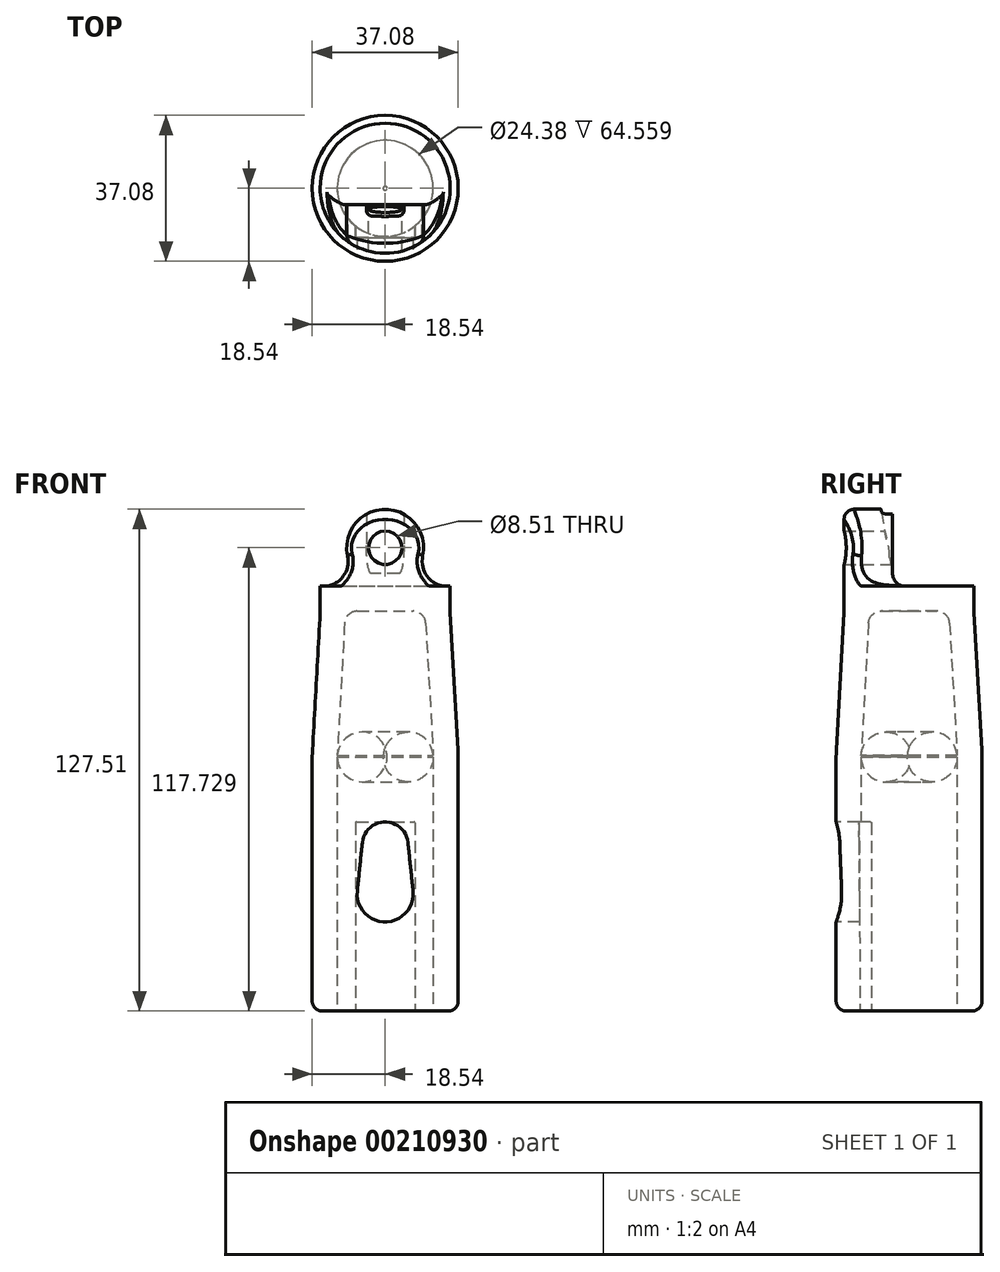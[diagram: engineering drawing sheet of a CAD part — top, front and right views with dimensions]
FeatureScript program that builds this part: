
annotation { "Feature Type Name" : "Feature", "Feature Type Description" : "" }
export const myFeature = defineFeature(function(context is Context, id is Id, definition is map)
    precondition{}
    {
        {
            var Q0;
            Q0=qCreatedBy(makeId("Front.planeOp"),FACE);
            var sketch = newSketch(context, id + "F0", { "sketchPlane" : qUnion([Q0])});
            skLineSegment(sketch, "E0", {"start": v(-18.54, -101.6) * mm, "end": v(-18.54, -38.1) * mm});
            skLineSegment(sketch, "E1", {"start": v(-18.46, -35.28) * mm, "end": v(-16.52, -0.35) * mm});
            skLineSegment(sketch, "E2", {"start": v(-16.51, 0) * mm, "end": v(-16.51, 6.35) * mm});
            skLineSegment(sketch, "E3", {"start": v(-16.51, 6.35) * mm, "end": v(0, 6.35) * mm});
            skLineSegment(sketch, "E4", {"start": v(-10.3, -3) * mm, "end": v(-12.18, -36.69) * mm});
            skLineSegment(sketch, "E5", {"start": v(-12.2, -37.04) * mm, "end": v(-12.2, -101.6) * mm});
            skLineSegment(sketch, "E6", {"start": v(-12.2, -101.6) * mm, "end": v(-18.54, -101.6) * mm});
            skLineSegment(sketch, "E7", {"start": v(0, 0) * mm, "end": v(0, 33.96) * mm, "construction": true});
            skLineSegment(sketch, "E8", {"start": v(0, 6.35) * mm, "end": v(0, 0) * mm});
            skLineSegment(sketch, "E9", {"start": v(0, 0) * mm, "end": v(-7.14, 0) * mm});
            skPoint(sketch, "E10.visualSharp", {"position": v(-16.51, -0.18) * mm});
            skArc(sketch, "E10.filletArc", {"start": v(-16.52, -0.35) * mm, "mid": v(-16.51, -0.18) * mm, "end": v(-16.51, 0) * mm});
            skPoint(sketch, "E11.visualSharp", {"position": v(-18.54, -36.69) * mm});
            skArc(sketch, "E11.filletArc", {"start": v(-18.46, -35.28) * mm, "mid": v(-18.52, -36.69) * mm, "end": v(-18.54, -38.1) * mm});
            skPoint(sketch, "E12.visualSharp", {"position": v(-12.2, -36.86) * mm});
            skArc(sketch, "E12.filletArc", {"start": v(-12.18, -36.69) * mm, "mid": v(-12.19, -36.86) * mm, "end": v(-12.2, -37.04) * mm});
            skPoint(sketch, "E13.visualSharp", {"position": v(-10.14, 0) * mm});
            skArc(sketch, "E13.filletArc", {"start": v(-7.14, 0) * mm, "mid": v(-9.32, -0.87) * mm, "end": v(-10.3, -3) * mm});
            skSolve(sketch);
        }
        {
            var Q0;
            Q0=makeQuery(id+"F0.imprint","IMPRINT",FACE,{"disambiguationData":[TD([[makeQuery(id+"F0.imprint","IMPRINT",EDGE,{"derivedFrom":sQuery(id+"F0.wireOp",EDGE,"E0")}),-1.0]])]});
            var Q1;
            Q1=sQuery(id+"F0.wireOp",EDGE,"E7");
            revolve(context, id + "F1", {"entities" : qUnion([Q0]), "axis" : qUnion([Q1]), "revolveType" : RevolveType.FULL});
        }
        {
            var Q0;
            Q0=qCreatedBy(makeId("Front.planeOp"),FACE);
            var sketch = newSketch(context, id + "F2", { "sketchPlane" : qUnion([Q0])});
            skLineSegment(sketch, "E14.0", {"start": v(16.51, 6.35) * mm, "end": v(-16.51, 6.35) * mm});
            skLineSegment(sketch, "E15", {"start": v(0, 6.35) * mm, "end": v(0, 16.13) * mm, "construction": true});
            skArc(sketch, "E16", {"start": v(9.55, 14.02) * mm, "mid": v(0, 25.9) * mm, "end": v(-9.55, 14.02) * mm});
            skArc(sketch, "E17", {"start": v(-16.51, 6.35) * mm, "mid": v(-11.05, 8.39) * mm, "end": v(-9.55, 14.02) * mm});
            skLineSegment(sketch, "E18", {"start": v(-15.75, 12.65) * mm, "end": v(15.75, 12.65) * mm, "construction": true});
            skArc(sketch, "E19", {"start": v(9.55, 14.02) * mm, "mid": v(11.05, 8.39) * mm, "end": v(16.51, 6.35) * mm});
            skCircle(sketch, "E20", {"center": v(0, 16.13) * mm, "radius": 4.25 * mm});
            skSolve(sketch);
        }
        {
            var Q0;
            Q0=makeQuery(id+"F2.imprint","IMPRINT",FACE,{"disambiguationData":[TD([[makeQuery(id+"F2.imprint","IMPRINT",EDGE,{"derivedFrom":sQuery(id+"F2.wireOp",EDGE,"E14.0")}),-1.0]])]});
            var Q1;
            Q1=makeQuery(id+"F1.opRevolve","SWEPT_FACE",FACE,{"disambiguationData":[OSD([sQuery(id+"F0.wireOp",EDGE,"E2")])]});
            extrude(context, id + "F3", {"entities" : qUnion([Q0]), "operationType" : NewBodyOperationType.ADD, "endBound" : BoundingType.UP_TO_SURFACE, "endBoundEntityFace" : qUnion([Q1]), "depth" : 19.05 * mm});
        }
        {
            var Q0;
            Q0=qCreatedBy(makeId("Right.planeOp"),FACE);
            var sketch = newSketch(context, id + "F4", { "sketchPlane" : qUnion([Q0])});
            skLineSegment(sketch, "E21", {"start": v(4.2, 25.9) * mm, "end": v(4.2, 9.52) * mm});
            skLineSegment(sketch, "E22", {"start": v(1.02, 6.35) * mm, "end": v(-1.02, 6.35) * mm});
            skLineSegment(sketch, "E23", {"start": v(-4.2, 9.52) * mm, "end": v(-4.2, 25.9) * mm});
            skLineSegment(sketch, "E24", {"start": v(-4.2, 25.9) * mm, "end": v(4.2, 25.9) * mm});
            skLineSegment(sketch, "E25", {"start": v(0, 6.35) * mm, "end": v(0, 25.9) * mm});
            skLineSegment(sketch, "E26", {"start": v(-16.51, 25.9) * mm, "end": v(16.5, 25.9) * mm});
            skLineSegment(sketch, "E27", {"start": v(16.51, 42.72) * mm, "end": v(16.51, 25.9) * mm});
            skLineSegment(sketch, "E28", {"start": v(-16.51, 25.9) * mm, "end": v(-16.51, 42.72) * mm});
            skPoint(sketch, "E29.visualSharp", {"position": v(4.2, 6.35) * mm});
            skArc(sketch, "E29.filletArc", {"start": v(1.02, 6.35) * mm, "mid": v(3.26, 7.28) * mm, "end": v(4.2, 9.52) * mm});
            skPoint(sketch, "E30.visualSharp", {"position": v(-4.2, 6.35) * mm});
            skArc(sketch, "E30.filletArc", {"start": v(-4.2, 9.52) * mm, "mid": v(-3.26, 7.28) * mm, "end": v(-1.02, 6.35) * mm});
            skPoint(sketch, "E31.0", {"position": v(0, 6.35) * mm});
            skLineSegment(sketch, "E32.0", {"start": v(6.92, 6.35) * mm, "end": v(-6.92, 6.35) * mm});
            skSolve(sketch);
        }
        {
            var Q0;
            Q0 = qSketchRegion(id + "F4", true);
            extrude(context, id + "F5", {"entities" : qUnion([Q0]), "operationType" : NewBodyOperationType.REMOVE, "endBound" : BoundingType.THROUGH_ALL, "oppositeDirection" : true, "depth" : 25.4 * mm, "hasSecondDirection" : true, "secondDirectionBound" : SecondDirectionBoundingType.THROUGH_ALL, "secondDirectionOppositeDirection" : false, "secondDirectionDepth" : 25.4 * mm});
        }
        {
            var Q0;
            Q0=qCreatedBy(makeId("Front.planeOp"),FACE);
            cPlane(context, id + "F6", {"entities" : qUnion([Q0]), "cplaneType" : CPlaneType.OFFSET, "offset" : 25.4 * mm, "width" : 152.4 * mm, "height" : 152.4 * mm});
        }
        {
            var Q0;
            Q0=qCreatedBy(id+"F6.planeOp",FACE);
            var sketch = newSketch(context, id + "F7", { "sketchPlane" : qUnion([Q0])});
            skLineSegment(sketch, "E33", {"start": v(0, 0) * mm, "end": v(0, -101.6) * mm});
            skArc(sketch, "E34", {"start": v(-7.07, -71.1) * mm, "mid": v(0, -78.94) * mm, "end": v(7.07, -71.1) * mm});
            skArc(sketch, "E35", {"start": v(5.81, -58.79) * mm, "mid": v(0, -53.54) * mm, "end": v(-5.81, -58.79) * mm});
            skLineSegment(sketch, "E36", {"start": v(-5.81, -58.79) * mm, "end": v(-7.07, -71.1) * mm});
            skLineSegment(sketch, "E37", {"start": v(5.81, -58.79) * mm, "end": v(7.07, -71.1) * mm});
            skLineSegment(sketch, "E38.0", {"start": v(18.54, -101.6) * mm, "end": v(-18.54, -101.6) * mm});
            skLineSegment(sketch, "E39", {"start": v(-18.54, -101.6) * mm, "end": v(-18.54, -44.52) * mm});
            skLineSegment(sketch, "E40", {"start": v(18.54, -50.67) * mm, "end": v(18.54, -103.33) * mm});
            skSolve(sketch);
        }
        {
            var Q0;
            {var subQ5=sQuery(id+"F7.wireOp",EDGE,"E36");Q0=makeQuery(id+"F7.imprint","IMPRINT",FACE,{"disambiguationData":[TD([[makeQuery(id+"F7.imprint","IMPRINT",EDGE,{"derivedFrom":subQ5}),1.0]])]});}
            var Q1;
            {var subQ5=sQuery(id+"F7.wireOp",EDGE,"E37");Q1=makeQuery(id+"F7.imprint","IMPRINT",FACE,{"disambiguationData":[TD([[makeQuery(id+"F7.imprint","IMPRINT",EDGE,{"derivedFrom":subQ5}),-1.0]])]});}
            var Q2;
            Q2=makeQuery(id+"F1.opRevolve","SWEPT_FACE",FACE,{"disambiguationData":[OSD([sQuery(id+"F0.wireOp",EDGE,"E5")])]});
            extrude(context, id + "F8", {"entities" : qUnion([Q0, Q1]), "operationType" : NewBodyOperationType.REMOVE, "endBound" : BoundingType.UP_TO_SURFACE, "oppositeDirection" : true, "endBoundEntityFace" : qUnion([Q2]), "depth" : 25.4 * mm});
        }
        {
            var Q0;
            Q0=qCreatedBy(makeId("Right.planeOp"),FACE);
            var sketch = newSketch(context, id + "F9", { "sketchPlane" : qUnion([Q0])});
            skLineSegment(sketch, "E41.0", {"start": v(-4.2, 14.02) * mm, "end": v(-4.2, 25.9) * mm, "construction": true});
            skLineSegment(sketch, "E42.0", {"start": v(-4.2, 9.52) * mm, "end": v(-4.2, 14.02) * mm, "construction": true});
            skLineSegment(sketch, "E43.0", {"start": v(4.2, 14.02) * mm, "end": v(4.2, 9.53) * mm, "construction": true});
            skLineSegment(sketch, "E44.0", {"start": v(4.2, 14.02) * mm, "end": v(4.2, 25.9) * mm, "construction": true});
            skLineSegment(sketch, "E45", {"start": v(-16.51, 25.9) * mm, "end": v(-16.51, 42.72) * mm});
            skLineSegment(sketch, "E46", {"start": v(-16.51, 25.9) * mm, "end": v(-4.2, 25.9) * mm});
            skLineSegment(sketch, "E47", {"start": v(4.2, 25.9) * mm, "end": v(16.5, 25.9) * mm});
            skLineSegment(sketch, "E48", {"start": v(16.51, 42.72) * mm, "end": v(16.51, 25.9) * mm});
            skLineSegment(sketch, "E49", {"start": v(-7.14, 25.9) * mm, "end": v(-4.2, 9.52) * mm});
            skLineSegment(sketch, "E50", {"start": v(4.2, 9.52) * mm, "end": v(7.14, 25.9) * mm});
            skLineSegment(sketch, "E51", {"start": v(-7.14, 25.9) * mm, "end": v(7.14, 25.9) * mm});
            skLineSegment(sketch, "E52", {"start": v(4.2, 9.52) * mm, "end": v(-4.2, 9.52) * mm});
            skLineSegment(sketch, "E53", {"start": v(0, 9.52) * mm, "end": v(0, 25.9) * mm, "construction": true});
            skPoint(sketch, "E54", {"position": v(10.35, 25.9) * mm});
            skLineSegment(sketch, "E55", {"start": v(18.54, -52.53) * mm, "end": v(18.54, -103.33) * mm, "construction": true});
            skSolve(sketch);
        }
        {
            var Q0;
            Q0=makeQuery(id+"F9.imprint","IMPRINT",FACE,{"disambiguationData":[TD([[makeQuery(id+"F9.imprint","IMPRINT",EDGE,{"derivedFrom":sQuery(id+"F9.wireOp",EDGE,"naz1NqcU-oahG-V51I-Ea1M-vouIKLxolOkW")}),-1.0]])]});
            var Q1;
            {var subQ3=sQuery(id+"F9.wireOp",EDGE,"E49");Q1=makeQuery(id+"F9.imprint","IMPRINT",FACE,{"disambiguationData":[TD([[makeQuery(id+"F9.imprint","IMPRINT",EDGE,{"derivedFrom":subQ3}),1.0]])]});}
            extrude(context, id + "F10", {"entities" : qUnion([Q0, Q1]), "operationType" : NewBodyOperationType.REMOVE, "endBound" : BoundingType.SYMMETRIC, "depth" : 9.52 * mm});
        }
        {
            var Q0;
            Q0=qCreatedBy(makeId("Right.planeOp"),FACE);
            var sketch = newSketch(context, id + "F11", { "sketchPlane" : qUnion([Q0])});
            skLineSegment(sketch, "E56", {"start": v(-12.2, -103.33) * mm, "end": v(-12.2, -52.63) * mm, "construction": true});
            skLineSegment(sketch, "E57", {"start": v(-18.54, -103.33) * mm, "end": v(-18.54, -52.53) * mm, "construction": true});
            skLineSegment(sketch, "E58", {"start": v(-19.05, -53.54) * mm, "end": v(-12.7, -53.54) * mm, "construction": true});
            skLineSegment(sketch, "E59.0", {"start": v(18.54, -101.6) * mm, "end": v(-18.54, -101.6) * mm, "construction": true});
            skLineSegment(sketch, "E60", {"start": v(-12.7, -53.54) * mm, "end": v(-12.45, -101.6) * mm});
            skLineSegment(sketch, "E61", {"start": v(-12.45, -101.6) * mm, "end": v(0, -101.6) * mm});
            skLineSegment(sketch, "E62", {"start": v(0, -101.6) * mm, "end": v(0, -53.54) * mm});
            skLineSegment(sketch, "E63", {"start": v(0, -53.54) * mm, "end": v(-12.7, -53.54) * mm});
            skSolve(sketch);
        }
        {
            var Q0;
            Q0=makeQuery(id+"F11.imprint","IMPRINT",FACE,{"disambiguationData":[TD([[makeQuery(id+"F11.imprint","IMPRINT",EDGE,{"derivedFrom":sQuery(id+"F11.wireOp",EDGE,"E60")}),1.0]])]});
            extrude(context, id + "F12", {"entities" : qUnion([Q0]), "operationType" : NewBodyOperationType.REMOVE, "endBound" : BoundingType.SYMMETRIC, "oppositeDirection" : true, "depth" : 15.08 * mm});
        }
        {
            var Q0;
            Q0=makeQuery(id+"F12.boolean.opBoolean","COPY",EDGE,{"derivedFrom":makeQuery(id+"F12.opExtrude","CAP_EDGE",EDGE,{"disambiguationData":[OSD([sQuery(id+"F11.wireOp",EDGE,"E60")])],"isStart":true})});
            var Q1;
            {var subQ0=sQuery(id+"F11.wireOp",EDGE,"E60");var subQ1=sQuery(id+"F11.wireOp",EDGE,"E63");Q1=makeQuery(id+"F12.boolean.opBoolean","COPY",EDGE,{"disambiguationData":[TD([makeQuery(id+"F12.opExtrude","CAP_FACE",FACE,{"disambiguationData":[OSD([subQ0,sQuery(id+"F11.wireOp",EDGE,"E61"),sQuery(id+"F11.wireOp",EDGE,"E62"),subQ1])],"isStart":true})])],"derivedFrom":makeQuery(id+"F12.opExtrude","SWEPT_EDGE",EDGE,{"disambiguationData":[OSD([subQ0,subQ1])]})});}
            var Q2;
            Q2=makeQuery(id+"F12.boolean.opBoolean","COPY",EDGE,{"derivedFrom":makeQuery(id+"F12.opExtrude","CAP_EDGE",EDGE,{"disambiguationData":[OSD([sQuery(id+"F11.wireOp",EDGE,"E63")])],"isStart":true})});
            var Q3;
            {var subQ0=sQuery(id+"F11.wireOp",EDGE,"E60");var subQ1=sQuery(id+"F11.wireOp",EDGE,"E63");Q3=makeQuery(id+"F12.boolean.opBoolean","COPY",EDGE,{"disambiguationData":[TD([makeQuery(id+"F12.opExtrude","CAP_FACE",FACE,{"disambiguationData":[OSD([subQ0,sQuery(id+"F11.wireOp",EDGE,"E61"),sQuery(id+"F11.wireOp",EDGE,"E62"),subQ1])],"isStart":false})])],"derivedFrom":makeQuery(id+"F12.opExtrude","SWEPT_EDGE",EDGE,{"disambiguationData":[OSD([subQ0,subQ1])]})});}
            var Q4;
            Q4=makeQuery(id+"F12.boolean.opBoolean","COPY",EDGE,{"derivedFrom":makeQuery(id+"F12.opExtrude","CAP_EDGE",EDGE,{"disambiguationData":[OSD([sQuery(id+"F11.wireOp",EDGE,"E60")])],"isStart":false})});
            var Q5;
            Q5=makeQuery(id+"F12.boolean.opBoolean","COPY",EDGE,{"derivedFrom":makeQuery(id+"F12.opExtrude","CAP_EDGE",EDGE,{"disambiguationData":[OSD([sQuery(id+"F11.wireOp",EDGE,"E63")])],"isStart":false})});
            fillet(context, id + "F13", {"entities" : qUnion([Q0, Q1, Q2, Q3, Q4, Q5]), "radius" : 0.25 * mm, "tangentPropagation" : true, "allowEdgeOverflow" : false});
        }
        {
            var Q0;
            Q0=makeQuery(id+"F10.boolean.opBoolean","COPY",EDGE,{"derivedFrom":makeQuery(id+"F10.opExtrude","CAP_EDGE",EDGE,{"disambiguationData":[OSD([sQuery(id+"F9.wireOp",EDGE,"E49")])],"isStart":false})});
            var Q1;
            {var subQ1=sQuery(id+"F9.wireOp",EDGE,"E49");Q1=makeQuery(id+"F10.boolean.opBoolean","COPY",EDGE,{"disambiguationData":[TD([makeQuery(id+"F5.boolean.opBoolean","COPY",FACE,{"derivedFrom":makeQuery(id+"F5.opExtrude","SWEPT_FACE",FACE,{"disambiguationData":[OSD([sQuery(id+"F4.wireOp",EDGE,"E23")])]})})])],"derivedFrom":makeQuery(id+"F10.opExtrude","CAP_EDGE",EDGE,{"disambiguationData":[OSD([subQ1])],"isStart":false})});}
            var Q2;
            Q2=makeQuery(id+"F10.boolean.opBoolean","COPY",EDGE,{"derivedFrom":makeQuery(id+"F10.opExtrude","CAP_EDGE",EDGE,{"disambiguationData":[OSD([sQuery(id+"F9.wireOp",EDGE,"E49")])],"isStart":true})});
            var Q3;
            {var subQ0=sQuery(id+"F9.wireOp",EDGE,"E49");Q3=makeQuery(id+"F10.boolean.opBoolean","COPY",EDGE,{"disambiguationData":[TD([makeQuery(id+"F5.boolean.opBoolean","COPY",FACE,{"derivedFrom":makeQuery(id+"F5.opExtrude","SWEPT_FACE",FACE,{"disambiguationData":[OSD([sQuery(id+"F4.wireOp",EDGE,"E23")])]})})])],"derivedFrom":makeQuery(id+"F10.opExtrude","CAP_EDGE",EDGE,{"disambiguationData":[OSD([subQ0])],"isStart":true})});}
            var Q4;
            Q4=makeQuery(id+"F10.boolean.opBoolean","COPY",EDGE,{"derivedFrom":makeQuery(id+"F10.opExtrude","CAP_EDGE",EDGE,{"disambiguationData":[OSD([sQuery(id+"F9.wireOp",EDGE,"E50")])],"isStart":true})});
            var Q5;
            {var subQ1=sQuery(id+"F9.wireOp",EDGE,"E50");Q5=makeQuery(id+"F10.boolean.opBoolean","COPY",EDGE,{"disambiguationData":[TD([makeQuery(id+"F5.boolean.opBoolean","COPY",FACE,{"derivedFrom":makeQuery(id+"F5.opExtrude","SWEPT_FACE",FACE,{"disambiguationData":[OSD([sQuery(id+"F4.wireOp",EDGE,"E21")])]})})])],"derivedFrom":makeQuery(id+"F10.opExtrude","CAP_EDGE",EDGE,{"disambiguationData":[OSD([subQ1])],"isStart":true})});}
            var Q6;
            {var subQ1=sQuery(id+"F9.wireOp",EDGE,"E50");Q6=makeQuery(id+"F10.boolean.opBoolean","COPY",EDGE,{"disambiguationData":[TD([makeQuery(id+"F5.boolean.opBoolean","COPY",FACE,{"derivedFrom":makeQuery(id+"F5.opExtrude","SWEPT_FACE",FACE,{"disambiguationData":[OSD([sQuery(id+"F4.wireOp",EDGE,"E21")])]})})])],"derivedFrom":makeQuery(id+"F10.opExtrude","CAP_EDGE",EDGE,{"disambiguationData":[OSD([subQ1])],"isStart":false})});}
            var Q7;
            Q7=makeQuery(id+"F10.boolean.opBoolean","COPY",EDGE,{"derivedFrom":makeQuery(id+"F10.opExtrude","CAP_EDGE",EDGE,{"disambiguationData":[OSD([sQuery(id+"F9.wireOp",EDGE,"E50")])],"isStart":false})});
            fillet(context, id + "F14", {"entities" : qUnion([Q0, Q1, Q2, Q3, Q4, Q5, Q6, Q7]), "radius" : 1.27 * mm, "tangentPropagation" : true, "allowEdgeOverflow" : false});
        }
        {
            var Q0;
            Q0=makeQuery(id+"F1.opRevolve","SWEPT_EDGE",EDGE,{"disambiguationData":[OSD([sQuery(id+"F0.wireOp",EDGE,"E0"),sQuery(id+"F0.wireOp",EDGE,"E6")])]});
            fillet(context, id + "F15", {"entities" : qUnion([Q0]), "radius" : 2.54 * mm, "tangentPropagation" : true, "allowEdgeOverflow" : false});
        }
        {
            var Q0;
            Q0=makeQuery(id+"F3.opExtrude","CAP_EDGE",EDGE,{"disambiguationData":[OSD([sQuery(id+"F2.wireOp",EDGE,"E16")])],"isStart":false});
            var Q1;
            Q1=makeQuery(id+"FDyp32CZKHexZ70_1.1.F3.opExtrude","CAP_EDGE",EDGE,{"disambiguationData":[OSD([sQuery(id+"F2.wireOp",EDGE,"E16")])],"isStart":false});
            fillet(context, id + "F16", {"entities" : qUnion([Q0, Q1]), "radius" : 2.54 * mm, "tangentPropagation" : true, "allowEdgeOverflow" : false});
        }
    });
